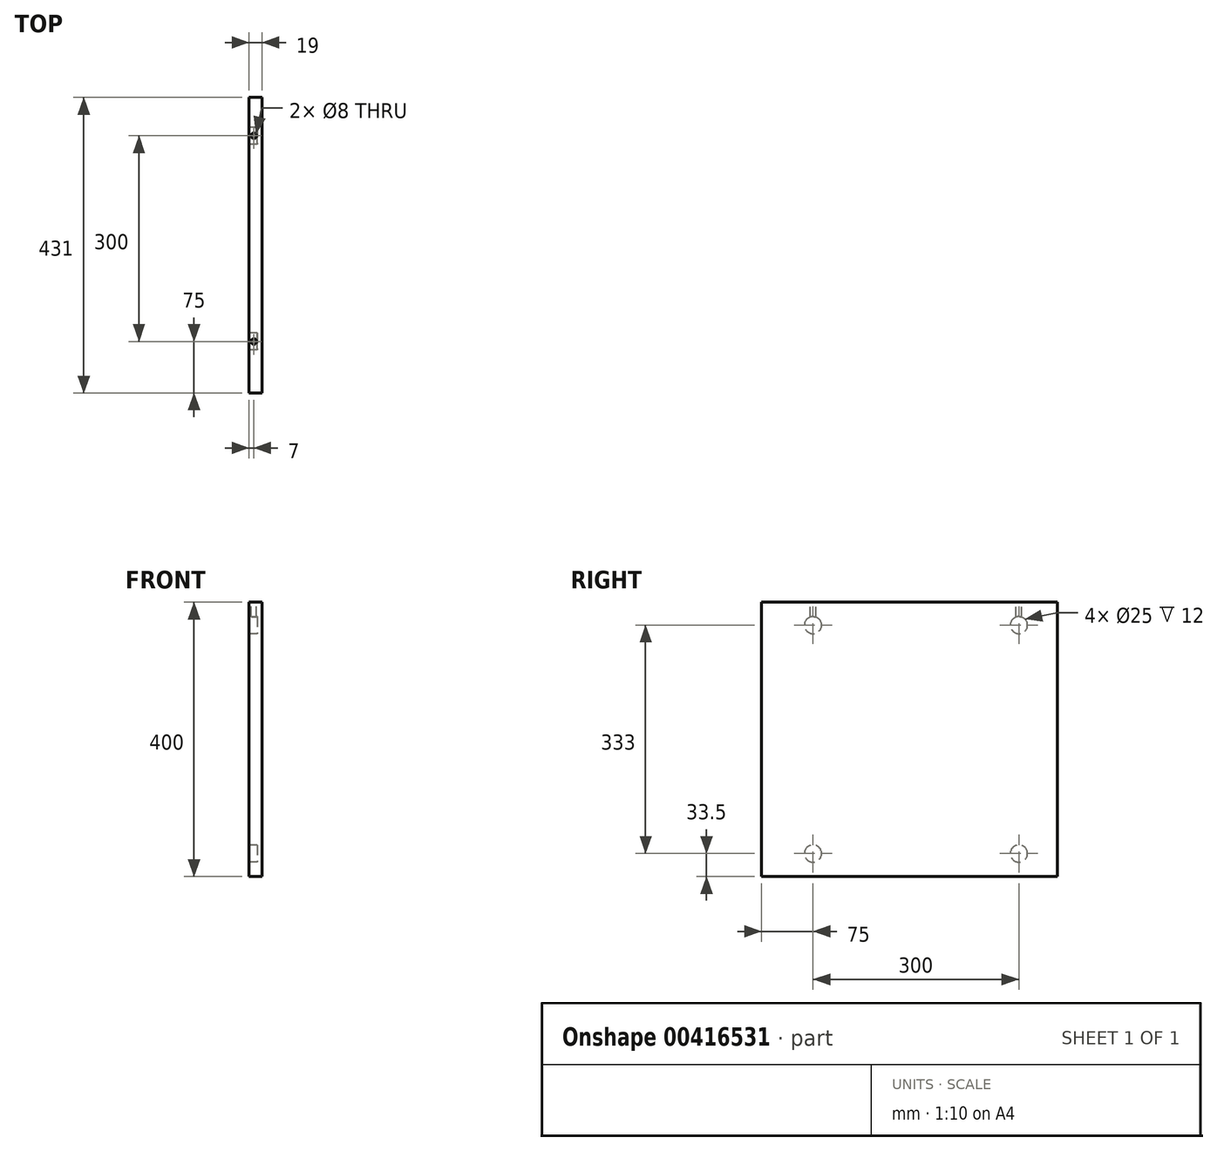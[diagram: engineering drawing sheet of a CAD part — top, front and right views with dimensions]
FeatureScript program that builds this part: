
annotation { "Feature Type Name" : "Feature", "Feature Type Description" : "" }
export const myFeature = defineFeature(function(context is Context, id is Id, definition is map)
    precondition{}
    {
        {
            var Q0;
            Q0=qCreatedBy(makeId("Right.planeOp"),FACE);
            var sketch = newSketch(context, id + "F0", { "sketchPlane" : qUnion([Q0])});
            skLineSegment(sketch, "E0.bottom", {"start": v(-215.5, -200) * mm, "end": v(215.5, -200) * mm});
            skLineSegment(sketch, "E0.top", {"start": v(-215.5, 200) * mm, "end": v(215.5, 200) * mm});
            skLineSegment(sketch, "E0.left", {"start": v(-215.5, -200) * mm, "end": v(-215.5, 200) * mm});
            skLineSegment(sketch, "E0.right", {"start": v(215.5, -200) * mm, "end": v(215.5, 200) * mm});
            skPoint(sketch, "E0.middle", {"position": v(0, 0) * mm});
            skSolve(sketch);
        }
        {
            var Q0;
            Q0 = qSketchRegion(id + "F0", true);
            extrude(context, id + "F1", {"entities" : qUnion([Q0]), "depth" : 19 * mm});
        }
        {
            var Q0;
            Q0=makeQuery(id+"F1.opExtrude","CAP_FACE",FACE,{"disambiguationData":[OSD([sQuery(id+"F0.wireOp",EDGE,"E0.bottom"),sQuery(id+"F0.wireOp",EDGE,"E0.top"),sQuery(id+"F0.wireOp",EDGE,"E0.left"),sQuery(id+"F0.wireOp",EDGE,"E0.right")])],"isStart":true});
            var sketch = newSketch(context, id + "F2", { "sketchPlane" : qUnion([Q0])});
            skLineSegment(sketch, "E1", {"start": v(140.5, 296.18) * mm, "end": v(140.5, -301.46) * mm, "construction": true});
            skLineSegment(sketch, "E2", {"start": v(-159.5, 290.96) * mm, "end": v(-159.5, -315.54) * mm, "construction": true});
            skLineSegment(sketch, "E3", {"start": v(-251.73, 166.5) * mm, "end": v(249.96, 166.5) * mm, "construction": true});
            skLineSegment(sketch, "E4", {"start": v(-244.54, -166.5) * mm, "end": v(253.6, -166.5) * mm, "construction": true});
            skCircle(sketch, "E5", {"center": v(-159.5, 166.5) * mm, "radius": 12.5 * mm});
            skCircle(sketch, "E6", {"center": v(140.5, 166.5) * mm, "radius": 12.5 * mm});
            skCircle(sketch, "E7", {"center": v(140.5, -166.5) * mm, "radius": 12.5 * mm});
            skCircle(sketch, "E8", {"center": v(-159.5, -166.5) * mm, "radius": 12.5 * mm});
            skSolve(sketch);
        }
        {
            var Q0;
            Q0 = qSketchRegion(id + "F2", true);
            extrude(context, id + "F3", {"entities" : qUnion([Q0]), "operationType" : NewBodyOperationType.REMOVE, "oppositeDirection" : true, "depth" : 12 * mm});
        }
        {
            var Q0;
            Q0=makeQuery(id+"F1.opExtrude","SWEPT_FACE",FACE,{"disambiguationData":[OSD([sQuery(id+"F0.wireOp",EDGE,"E0.top")])]});
            var sketch = newSketch(context, id + "F4", { "sketchPlane" : qUnion([Q0])});
            skLineSegment(sketch, "E9", {"start": v(-12.25, 159.5) * mm, "end": v(34.7, 159.5) * mm, "construction": true});
            skLineSegment(sketch, "E10", {"start": v(-11.15, -140.5) * mm, "end": v(25.15, -140.5) * mm, "construction": true});
            skPoint(sketch, "E11", {"position": v(7, 159.5) * mm});
            skPoint(sketch, "E12", {"position": v(7, -140.5) * mm});
            skSolve(sketch);
        }
        {
            var Q0;
            Q0=sQuery(id+"F4.wireOp",VERTEX,"E11");
            var Q1;
            Q1=sQuery(id+"F4.wireOp",VERTEX,"E12");
            var Q2;
            Q2=makeQuery(id+"F1.opExtrude","SWEPT_BODY",BODY,{"disambiguationData":[OSD([sQuery(id+"F0.wireOp",EDGE,"E0.bottom"),sQuery(id+"F0.wireOp",EDGE,"E0.top"),sQuery(id+"F0.wireOp",EDGE,"E0.left"),sQuery(id+"F0.wireOp",EDGE,"E0.right")])]});
            hole(context, id + "F5", {"style" : HoleStyle.SIMPLE, "endStyle" : HoleEndStyle.BLIND, "holeDiameter" : 8 * mm, "holeDepth" : 22 * mm, "isTappedThrough" : true, "tappedDepth" : 12 * mm, "tapClearance" : 3, "startFromSketch" : true, "locations" : qUnion([Q0, Q1]), "scope" : qUnion([Q2])});
        }
    });
